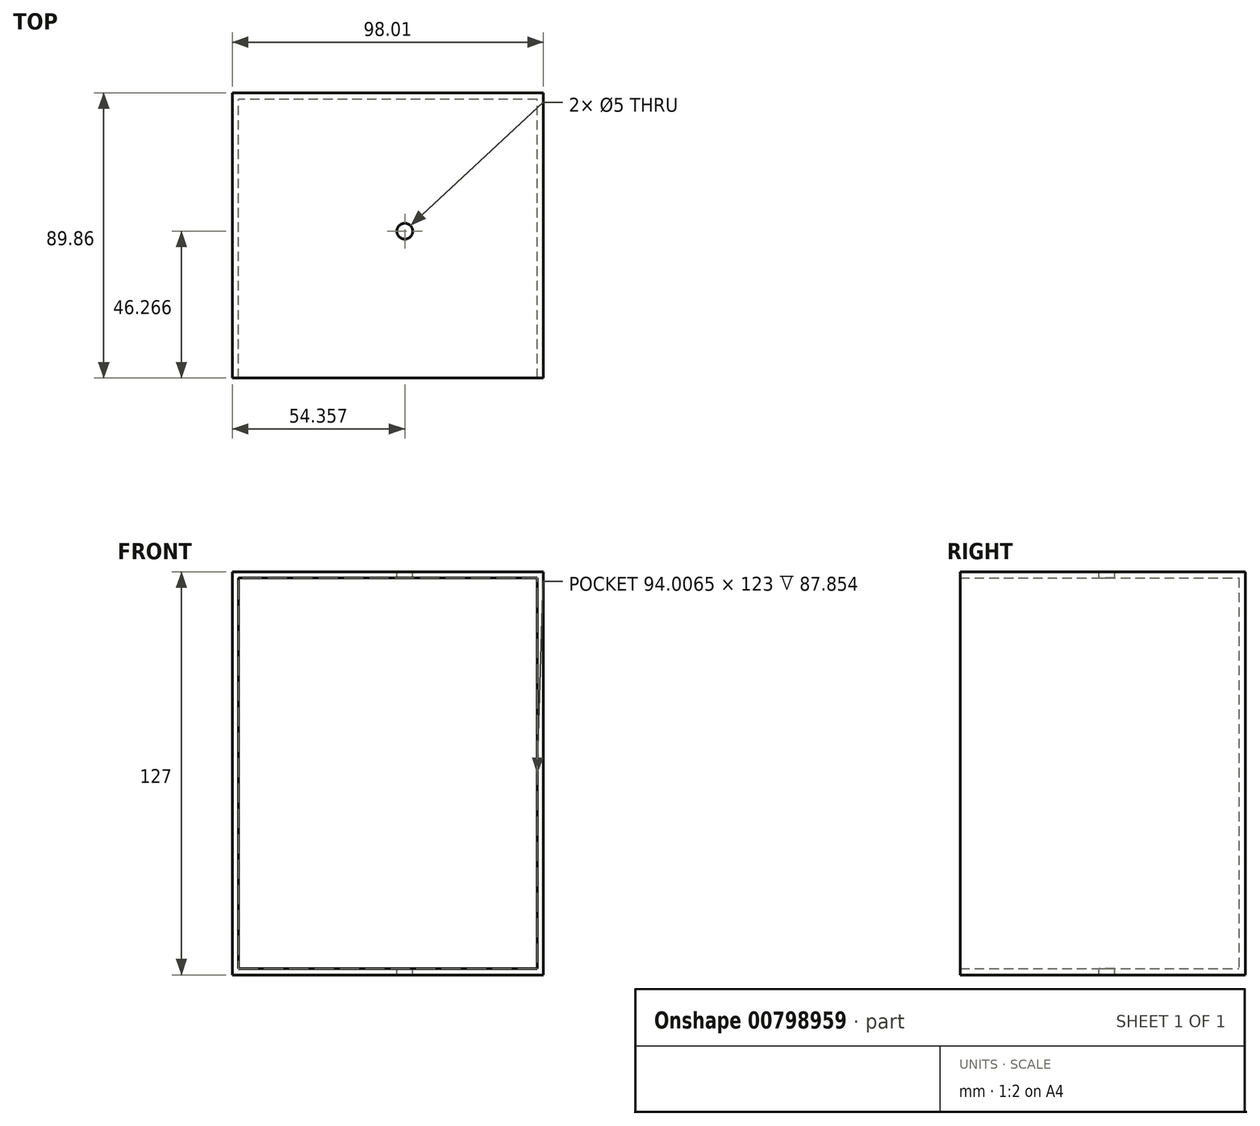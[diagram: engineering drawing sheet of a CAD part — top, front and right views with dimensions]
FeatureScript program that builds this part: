
annotation { "Feature Type Name" : "Feature", "Feature Type Description" : "" }
export const myFeature = defineFeature(function(context is Context, id is Id, definition is map)
    precondition{}
    {
        {
            var Q0;
            Q0=qCreatedBy(makeId("Top.planeOp"),FACE);
            var sketch = newSketch(context, id + "F0", { "sketchPlane" : qUnion([Q0])});
            skLineSegment(sketch, "E0.bottom", {"start": v(27.69, -30.12) * mm, "end": v(-70.32, -30.12) * mm});
            skLineSegment(sketch, "E0.top", {"start": v(27.69, 59.74) * mm, "end": v(-70.32, 59.74) * mm});
            skLineSegment(sketch, "E0.left", {"start": v(27.69, -30.12) * mm, "end": v(27.69, 59.74) * mm});
            skLineSegment(sketch, "E0.right", {"start": v(-70.32, -30.12) * mm, "end": v(-70.32, 59.74) * mm});
            skPoint(sketch, "E0.middle", {"position": v(-21.31, 14.81) * mm});
            skSolve(sketch);
        }
        {
            var Q0;
            Q0=makeQuery(id+"F0.imprint","IMPRINT",FACE,{"disambiguationData":[TD([[makeQuery(id+"F0.imprint","IMPRINT",EDGE,{"derivedFrom":sQuery(id+"F0.wireOp",EDGE,"E0.bottom")}),-1.0]])]});
            extrude(context, id + "F1", {"entities" : qUnion([Q0]), "depth" : 127 * mm, "offsetDistance" : 25.4 * mm});
        }
        {
            var Q0;
            Q0=makeQuery(id+"F1.opExtrude","CAP_FACE",FACE,{"disambiguationData":[OSD([sQuery(id+"F0.wireOp",EDGE,"E0.bottom"),sQuery(id+"F0.wireOp",EDGE,"E0.top"),sQuery(id+"F0.wireOp",EDGE,"E0.left"),sQuery(id+"F0.wireOp",EDGE,"E0.right")])],"isStart":false});
            var sketch = newSketch(context, id + "F2", { "sketchPlane" : qUnion([Q0])});
            skSolve(sketch);
        }
        {
            var Q0;
            Q0=makeQuery(id+"F2.imprint","IMPRINT",FACE,{"disambiguationData":[TD([[makeQuery(id+"F2.imprint","IMPRINT",EDGE,{"derivedFrom":makeQuery(id+"F1.opExtrude","CAP_EDGE",EDGE,{"disambiguationData":[OSD([sQuery(id+"F0.wireOp",EDGE,"E0.bottom")])],"isStart":false})}),-1.0]])]});
            var sketch = newSketch(context, id + "F3", { "sketchPlane" : qUnion([Q0])});
            skLineSegment(sketch, "E1.0", {"start": v(26.69, -29.12) * mm, "end": v(-69.32, -29.12) * mm});
            skLineSegment(sketch, "E1.1", {"start": v(26.69, -29.12) * mm, "end": v(26.69, 58.74) * mm});
            skLineSegment(sketch, "E1.2", {"start": v(26.69, 58.74) * mm, "end": v(-69.32, 58.74) * mm});
            skLineSegment(sketch, "E1.3", {"start": v(-69.32, -29.12) * mm, "end": v(-69.32, 58.74) * mm});
            skSolve(sketch);
        }
        {
            var Q0;
            Q0=makeQuery(id+"F3.imprint","IMPRINT",FACE,{"disambiguationData":[TD([[makeQuery(id+"F3.imprint","IMPRINT",EDGE,{"derivedFrom":sQuery(id+"F3.wireOp",EDGE,"E1.0")}),-1.0]])]});
            extrude(context, id + "F4", {"entities" : qUnion([Q0]), "operationType" : NewBodyOperationType.ADD, "oppositeDirection" : true, "depth" : 84.73 * mm, "offsetDistance" : 25 * mm});
        }
        {
            var Q0;
            Q0=makeQuery(id+"F1.opExtrude","SWEPT_FACE",FACE,{"disambiguationData":[OSD([sQuery(id+"F0.wireOp",EDGE,"E0.bottom")])]});
            shell(context, id + "F5", {"entities" : qUnion([Q0]), "thickness" : 2 * mm});
        }
        {
            var Q0;
            Q0=makeQuery(id+"F2.imprint","IMPRINT",FACE,{"disambiguationData":[TD([[makeQuery(id+"F2.imprint","IMPRINT",EDGE,{"derivedFrom":makeQuery(id+"F1.opExtrude","CAP_EDGE",EDGE,{"disambiguationData":[OSD([sQuery(id+"F0.wireOp",EDGE,"E0.bottom")])],"isStart":false})}),-1.0]])]});
            var sketch = newSketch(context, id + "F6", { "sketchPlane" : qUnion([Q0])});
            skCircle(sketch, "E2", {"center": v(-15.96, 16.15) * mm, "radius": 5.55 * mm});
            skSolve(sketch);
        }
        {
            var Q0;
            Q0=sQuery(id+"F6.wireOp",VERTEX,"E2.center");
            var Q1;
            Q1=makeQuery(id+"F1.opExtrude","SWEPT_BODY",BODY,{"disambiguationData":[OSD([sQuery(id+"F0.wireOp",EDGE,"E0.bottom"),sQuery(id+"F0.wireOp",EDGE,"E0.top"),sQuery(id+"F0.wireOp",EDGE,"E0.left"),sQuery(id+"F0.wireOp",EDGE,"E0.right")])]});
            hole(context, id + "F7", {"style" : HoleStyle.SIMPLE, "endStyle" : HoleEndStyle.THROUGH, "holeDiameter" : 5 * mm, "majorDiameter" : 5 * mm, "isTappedThrough" : true, "tappedDepth" : 12 * mm, "tapClearance" : 3, "locations" : qUnion([Q0]), "scope" : qUnion([Q1])});
        }
    });
